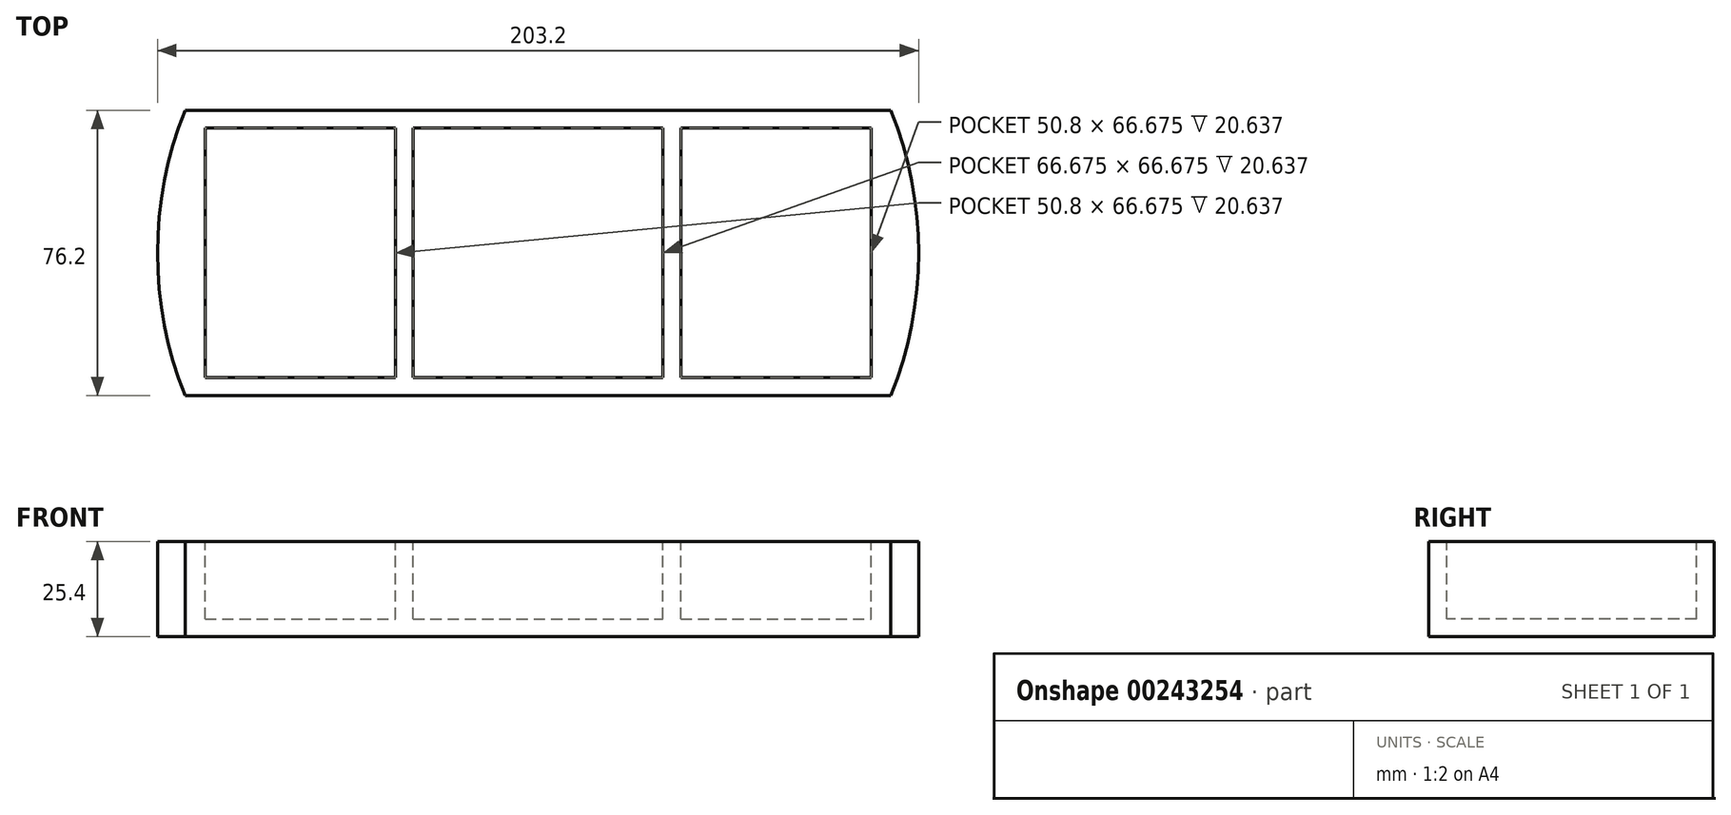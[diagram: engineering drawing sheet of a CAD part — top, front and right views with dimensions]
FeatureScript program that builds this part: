
annotation { "Feature Type Name" : "Feature", "Feature Type Description" : "" }
export const myFeature = defineFeature(function(context is Context, id is Id, definition is map)
    precondition{}
    {
        {
            var Q0;
            Q0=qCreatedBy(makeId("Top.planeOp"),FACE);
            var sketch = newSketch(context, id + "F0", { "sketchPlane" : qUnion([Q0])});
            skLineSegment(sketch, "E0.bottom", {"start": v(0, 0) * mm, "end": v(203.2, 0) * mm});
            skLineSegment(sketch, "E0.top", {"start": v(0, -76.2) * mm, "end": v(203.2, -76.2) * mm});
            skLineSegment(sketch, "E0.left", {"start": v(0, 0) * mm, "end": v(0, -76.2) * mm});
            skLineSegment(sketch, "E0.right", {"start": v(203.2, 0) * mm, "end": v(203.2, -76.2) * mm});
            skArc(sketch, "E1", {"start": v(7.41, 0) * mm, "mid": v(0, -38.1) * mm, "end": v(7.41, -76.2) * mm});
            skPoint(sketch, "E1.centerSnap0", {"position": v(0, -38.1) * mm});
            skPoint(sketch, "E1.centerSnap1", {"position": v(101.6, 0) * mm});
            skArc(sketch, "E2.trimOffspring", {"start": v(195.79, -76.2) * mm, "mid": v(203.2, -38.1) * mm, "end": v(195.79, 0) * mm});
            skSolve(sketch);
        }
        {
            var Q0;
            {var subQ0=sQuery(id+"F0.wireOp",EDGE,"E1");var subQ4=sQuery(id+"F0.wireOp",EDGE,"E0.bottom");var subQ5=makeQuery(id+"F0.imprint","INTERSECT",VERTEX,{"derivedFrom":[subQ4,subQ0]});Q0=makeQuery(id+"F0.imprint","IMPRINT",FACE,{"disambiguationData":[TD([[makeQuery(id+"F0.imprint","IMPRINT",EDGE,{"disambiguationData":[TD([[subQ5,-1.0]])],"derivedFrom":subQ4}),-1.0]])]});}
            extrude(context, id + "F1", {"entities" : qUnion([Q0]), "depth" : 25.4 * mm});
        }
        {
            var Q0;
            Q0=makeQuery(id+"F1.opExtrude","CAP_FACE",FACE,{"disambiguationData":[OSD([sQuery(id+"F0.wireOp",EDGE,"E0.bottom"),sQuery(id+"F0.wireOp",EDGE,"E0.top"),sQuery(id+"F0.wireOp",EDGE,"E1"),sQuery(id+"F0.wireOp",EDGE,"E2.trimOffspring")])],"isStart":false});
            var sketch = newSketch(context, id + "F2", { "sketchPlane" : qUnion([Q0])});
            skLineSegment(sketch, "E3", {"start": v(15.88, -71.44) * mm, "end": v(187.32, -71.44) * mm});
            skLineSegment(sketch, "E4", {"start": v(15.88, -4.76) * mm, "end": v(187.32, -4.76) * mm});
            skLineSegment(sketch, "E5", {"start": v(15.87, -4.76) * mm, "end": v(15.88, -71.44) * mm});
            skLineSegment(sketch, "E6", {"start": v(187.32, -4.76) * mm, "end": v(187.32, -71.44) * mm});
            skLineSegment(sketch, "E7", {"start": v(63.5, -4.76) * mm, "end": v(63.5, -71.44) * mm});
            skLineSegment(sketch, "E8", {"start": v(68.26, -4.76) * mm, "end": v(68.26, -71.44) * mm});
            skLineSegment(sketch, "E9", {"start": v(134.94, -4.76) * mm, "end": v(134.94, -71.44) * mm});
            skLineSegment(sketch, "E10", {"start": v(139.7, -4.76) * mm, "end": v(139.7, -71.44) * mm});
            skLineSegment(sketch, "E11", {"start": v(101.6, 0) * mm, "end": v(101.6, -76.2) * mm, "construction": true});
            skLineSegment(sketch, "E12", {"start": v(190.5, 0) * mm, "end": v(190.5, -76.2) * mm});
            skLineSegment(sketch, "E13", {"start": v(12.7, 0) * mm, "end": v(12.7, -76.2) * mm});
            skLineSegment(sketch, "E14", {"start": v(187.32, -4.76) * mm, "end": v(190.5, -4.76) * mm});
            skLineSegment(sketch, "E15", {"start": v(187.32, -71.44) * mm, "end": v(190.5, -71.44) * mm});
            skLineSegment(sketch, "E16", {"start": v(15.88, -4.76) * mm, "end": v(12.7, -4.76) * mm});
            skLineSegment(sketch, "E17", {"start": v(15.88, -71.44) * mm, "end": v(12.7, -71.44) * mm});
            skLineSegment(sketch, "E18", {"start": v(187.32, -71.44) * mm, "end": v(187.32, -76.2) * mm});
            skLineSegment(sketch, "E19", {"start": v(187.32, -4.76) * mm, "end": v(187.32, 0) * mm});
            skLineSegment(sketch, "E20", {"start": v(15.88, -4.76) * mm, "end": v(15.88, 0) * mm});
            skLineSegment(sketch, "E21", {"start": v(15.88, -71.44) * mm, "end": v(15.88, -76.2) * mm});
            skLineSegment(sketch, "E22", {"start": v(15.88, -76.2) * mm, "end": v(12.7, -76.2) * mm});
            skLineSegment(sketch, "E23", {"start": v(15.88, 0) * mm, "end": v(12.7, 0) * mm});
            skSolve(sketch);
        }
        {
            var Q0;
            {var subQ0=sQuery(id+"F2.wireOp",EDGE,"E5");Q0=makeQuery(id+"F2.imprint","IMPRINT",FACE,{"disambiguationData":[TD([[makeQuery(id+"F2.imprint","IMPRINT",EDGE,{"derivedFrom":subQ0}),1.0]])]});}
            var Q1;
            {var subQ0=sQuery(id+"F2.wireOp",EDGE,"E8");Q1=makeQuery(id+"F2.imprint","IMPRINT",FACE,{"disambiguationData":[TD([[makeQuery(id+"F2.imprint","IMPRINT",EDGE,{"derivedFrom":subQ0}),1.0]])]});}
            var Q2;
            {var subQ0=sQuery(id+"F2.wireOp",EDGE,"E6");Q2=makeQuery(id+"F2.imprint","IMPRINT",FACE,{"disambiguationData":[TD([[makeQuery(id+"F2.imprint","IMPRINT",EDGE,{"derivedFrom":subQ0}),-1.0]])]});}
            var Q3;
            Q3=makeQuery(id+"F2.imprint","IMPRINT",FACE,{"disambiguationData":[TD([[makeQuery(id+"F2.imprint","IMPRINT",EDGE,{"derivedFrom":sQuery(id+"F2.wireOp",EDGE,"E5")}),-1.0]])]});
            var Q4;
            Q4=makeQuery(id+"F2.imprint","IMPRINT",FACE,{"disambiguationData":[TD([[makeQuery(id+"F2.imprint","IMPRINT",EDGE,{"derivedFrom":sQuery(id+"F2.wireOp",EDGE,"E6")}),1.0]])]});
            extrude(context, id + "F3", {"entities" : qUnion([Q0, Q1, Q2, Q3, Q4]), "operationType" : NewBodyOperationType.REMOVE, "oppositeDirection" : true, "depth" : 20.64 * mm});
        }
    });
